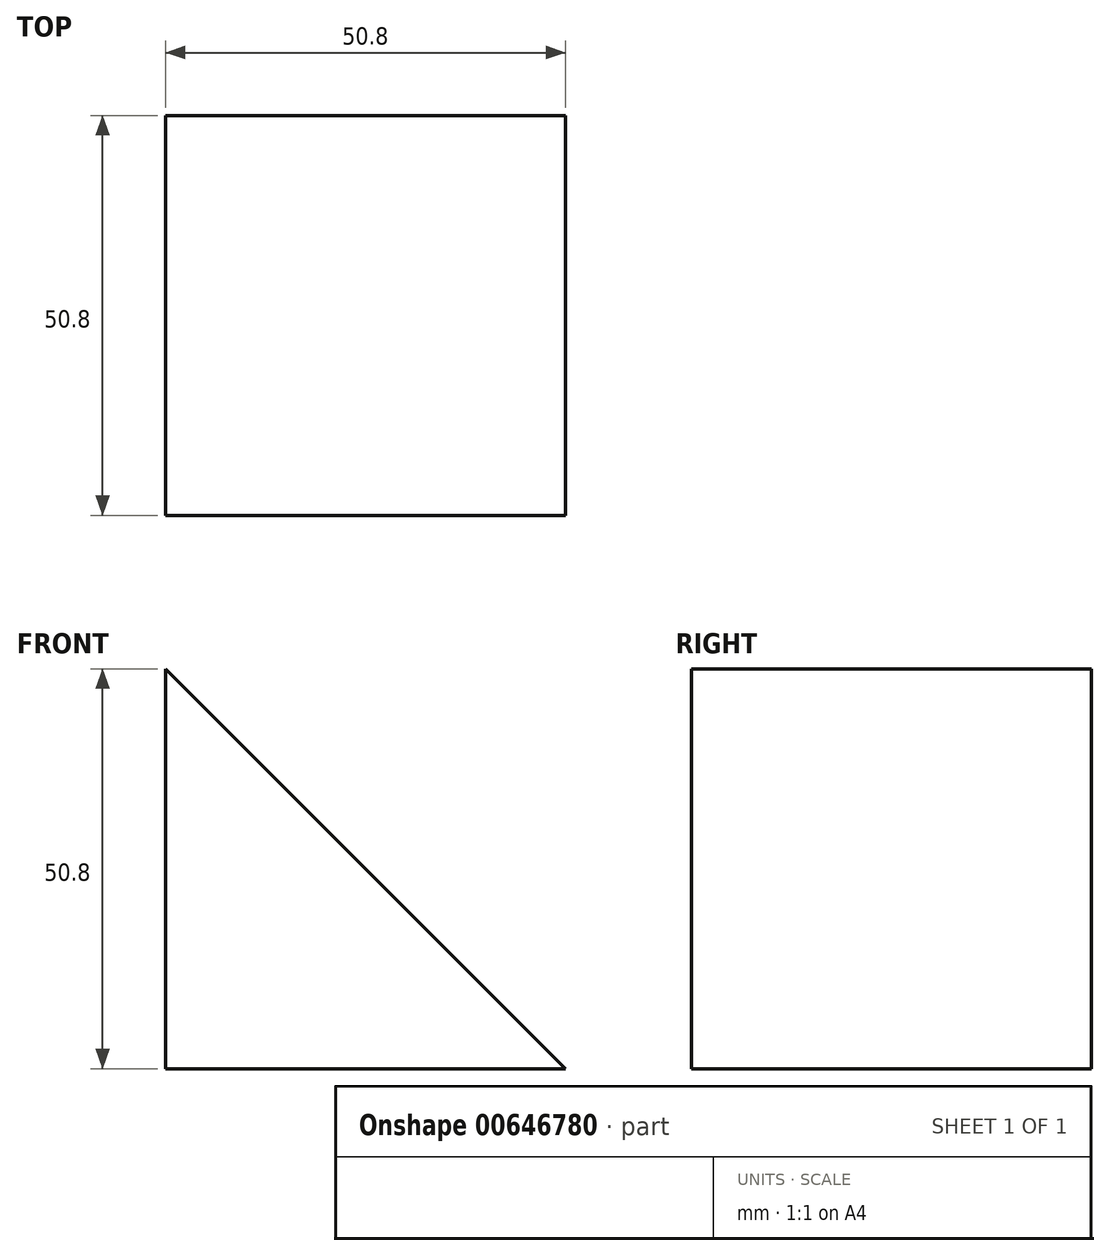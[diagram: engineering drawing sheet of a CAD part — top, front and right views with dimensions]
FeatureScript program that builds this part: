
annotation { "Feature Type Name" : "Feature", "Feature Type Description" : "" }
export const myFeature = defineFeature(function(context is Context, id is Id, definition is map)
    precondition{}
    {
        {
            var Q0;
            Q0=qCreatedBy(makeId("Front.planeOp"),FACE);
            var sketch = newSketch(context, id + "F0", { "sketchPlane" : qUnion([Q0])});
            skLineSegment(sketch, "E0", {"start": v(0, 0) * mm, "end": v(-50.8, 0) * mm});
            skLineSegment(sketch, "E1", {"start": v(-50.8, 0) * mm, "end": v(-50.8, 50.8) * mm});
            skLineSegment(sketch, "E2", {"start": v(-50.8, 50.8) * mm, "end": v(0, 0) * mm});
            skSolve(sketch);
        }
        {
            var Q0;
            Q0 = qSketchRegion(id + "F0", true);
            extrude(context, id + "F1", {"entities" : qUnion([Q0]), "depth" : 50.8 * mm, "offsetDistance" : 25.4 * mm});
        }
    });
